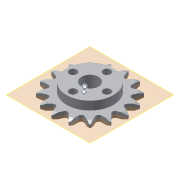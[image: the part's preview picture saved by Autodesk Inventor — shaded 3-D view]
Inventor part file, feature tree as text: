
AUTODESK INVENTOR PART (.ipt)
format: ipt  version: 2013 (Build 170138000, 138)  size: 412,672 bytes
history: native  units: in
note: dims shown in document units (in); Inventor stores cm internally (conversion verified against a paired STEP export)
features: other x17, plane x1
ambient origin geometry x8: Origin, YZ Plane, XZ Plane, XY Plane, X Axis, Y Axis, Z Axis, Center Point
bodies: Solid1 (feature_tree)
feature tree (18):
  other  "Tetrix sprocket 16T.ipt"
  other  "sprocket_25_16t_tetrix::Tetrix sprocket 16T.ipt"
  other  "TaggingFeature1"
  other  "FRONT"
  other  "TOP"
  other  "RIGHT"
  plane  "Work Plane4"
  other  "A_1"
  other  "A_2"
  other  "A_4"
  other  "A_5"
  other  "A_6"
  other  "A_3"
  other  "A_7"
  other  "A_8"
  other  "A_9"
  other  "iComposite:2"
  other  "iComposite:1"
